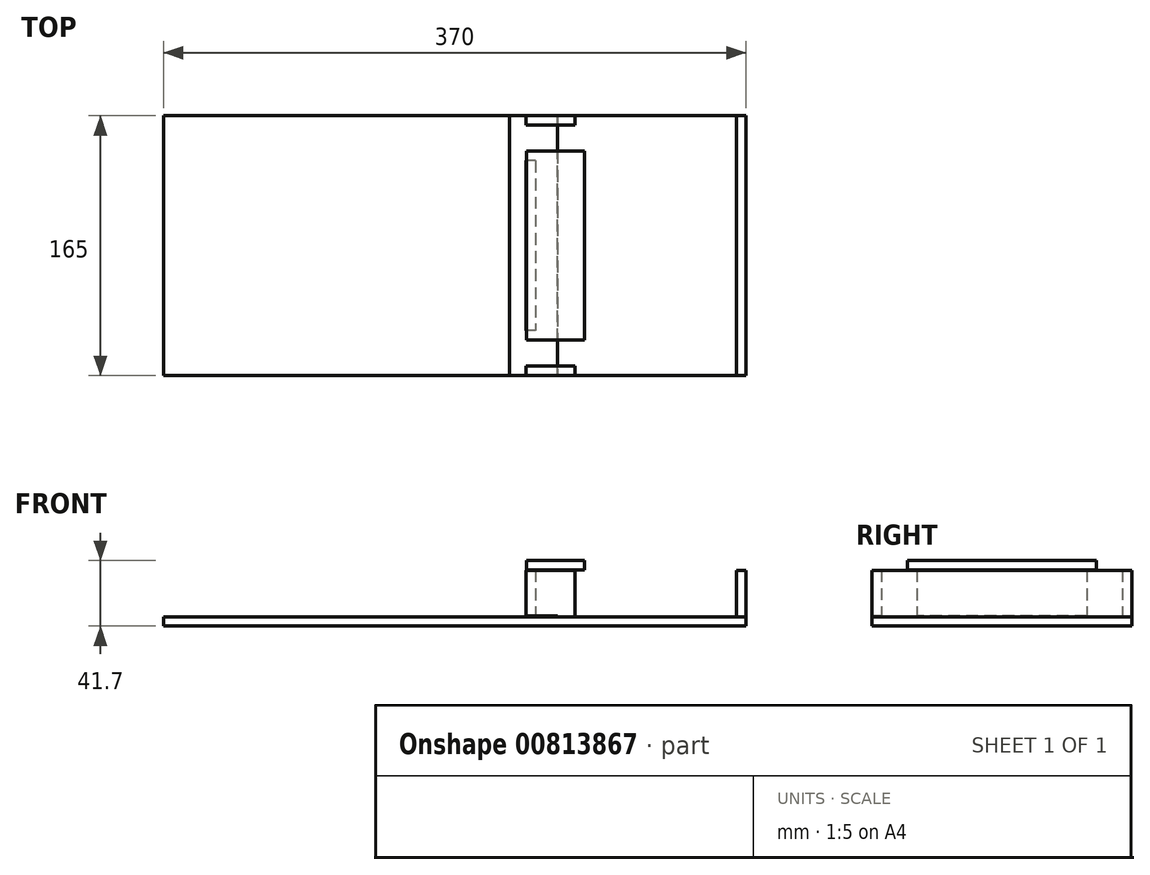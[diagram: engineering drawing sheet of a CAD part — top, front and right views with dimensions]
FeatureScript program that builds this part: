
annotation { "Feature Type Name" : "Feature", "Feature Type Description" : "" }
export const myFeature = defineFeature(function(context is Context, id is Id, definition is map)
    precondition{}
    {
        {
            var Q0;
            Q0=qCreatedBy(makeId("Top.planeOp"),FACE);
            var sketch = newSketch(context, id + "F0", { "sketchPlane" : qUnion([Q0])});
            skLineSegment(sketch, "E0.bottom", {"start": v(-185, 82.5) * mm, "end": v(185, 82.5) * mm});
            skLineSegment(sketch, "E0.top", {"start": v(-185, -82.5) * mm, "end": v(185, -82.5) * mm});
            skLineSegment(sketch, "E0.left", {"start": v(-185, 82.5) * mm, "end": v(-185, -82.5) * mm});
            skLineSegment(sketch, "E0.right", {"start": v(185, 82.5) * mm, "end": v(185, -82.5) * mm});
            skPoint(sketch, "E0.middle", {"position": v(0, 0) * mm});
            skSolve(sketch);
        }
        {
            var Q0;
            Q0 = qSketchRegion(id + "F0", true);
            extrude(context, id + "F1", {"entities" : qUnion([Q0]), "depth" : 6 * mm, "offsetDistance" : 25 * mm});
        }
        {
            var Q0;
            Q0=makeQuery(id+"F1.opExtrude","CAP_FACE",FACE,{"disambiguationData":[OSD([sQuery(id+"F0.wireOp",EDGE,"E0.bottom"),sQuery(id+"F0.wireOp",EDGE,"E0.top"),sQuery(id+"F0.wireOp",EDGE,"E0.left"),sQuery(id+"F0.wireOp",EDGE,"E0.right")])],"isStart":false});
            var sketch = newSketch(context, id + "F2", { "sketchPlane" : qUnion([Q0])});
            skLineSegment(sketch, "E1.bottom", {"start": v(185, 82.5) * mm, "end": v(179, 82.5) * mm});
            skLineSegment(sketch, "E1.top", {"start": v(185, -82.5) * mm, "end": v(179, -82.5) * mm});
            skLineSegment(sketch, "E1.left", {"start": v(185, 82.5) * mm, "end": v(185, -82.5) * mm});
            skLineSegment(sketch, "E1.right", {"start": v(179, 82.5) * mm, "end": v(179, -82.5) * mm});
            skSolve(sketch);
        }
        {
            var Q0;
            Q0 = qSketchRegion(id + "F2", true);
            extrude(context, id + "F3", {"entities" : qUnion([Q0]), "depth" : 29.5 * mm, "offsetDistance" : 25 * mm});
        }
        {
            var Q0;
            Q0=makeQuery(id+"F1.opExtrude","CAP_FACE",FACE,{"disambiguationData":[OSD([sQuery(id+"F0.wireOp",EDGE,"E0.bottom"),sQuery(id+"F0.wireOp",EDGE,"E0.top"),sQuery(id+"F0.wireOp",EDGE,"E0.left"),sQuery(id+"F0.wireOp",EDGE,"E0.right")])],"isStart":false});
            var sketch = newSketch(context, id + "F4", { "sketchPlane" : qUnion([Q0])});
            skLineSegment(sketch, "E2.bottom", {"start": v(76.46, -82.5) * mm, "end": v(45.46, -82.5) * mm});
            skLineSegment(sketch, "E2.top", {"start": v(76.46, -76.5) * mm, "end": v(45.46, -76.5) * mm});
            skLineSegment(sketch, "E2.left", {"start": v(76.46, -82.5) * mm, "end": v(76.46, -76.5) * mm});
            skLineSegment(sketch, "E2.right", {"start": v(45.46, -82.5) * mm, "end": v(45.46, -76.5) * mm});
            skLineSegment(sketch, "E3", {"start": v(-7.96, 0) * mm, "end": v(76.02, 0) * mm});
            skLineSegment(sketch, "E4.MirrorCS", {"start": v(76.46, 82.5) * mm, "end": v(45.46, 82.5) * mm});
            skLineSegment(sketch, "E5.MirrorCS", {"start": v(76.46, 76.5) * mm, "end": v(45.46, 76.5) * mm});
            skLineSegment(sketch, "E6.MirrorCS", {"start": v(45.46, 82.5) * mm, "end": v(45.46, 76.5) * mm});
            skLineSegment(sketch, "E7.MirrorCS", {"start": v(76.46, 82.5) * mm, "end": v(76.46, 76.5) * mm});
            skSolve(sketch);
        }
        {
            var Q0;
            Q0 = qSketchRegion(id + "F4", true);
            var Q1;
            Q1=makeQuery(id+"F3.opExtrude","CAP_FACE",FACE,{"disambiguationData":[OSD([sQuery(id+"F2.wireOp",EDGE,"E1.bottom"),sQuery(id+"F2.wireOp",EDGE,"E1.top"),sQuery(id+"F2.wireOp",EDGE,"E1.left"),sQuery(id+"F2.wireOp",EDGE,"E1.right")])],"isStart":false});
            extrude(context, id + "F5", {"entities" : qUnion([Q0]), "endBound" : BoundingType.UP_TO_SURFACE, "depth" : 27 * mm, "endBoundEntityFace" : qUnion([Q1]), "offsetDistance" : 25 * mm});
        }
        {
            var Q0;
            Q0=qCreatedBy(makeId("Front.planeOp"),FACE);
            var sketch = newSketch(context, id + "F6", { "sketchPlane" : qUnion([Q0])});
            skLineSegment(sketch, "E8.bottom", {"start": v(34.83, 5.98) * mm, "end": v(65.46, 5.98) * mm});
            skLineSegment(sketch, "E8.top", {"start": v(34.83, 6.48) * mm, "end": v(65.46, 6.48) * mm});
            skLineSegment(sketch, "E8.left", {"start": v(34.83, 5.98) * mm, "end": v(34.83, 6.48) * mm});
            skLineSegment(sketch, "E8.right", {"start": v(65.46, 5.98) * mm, "end": v(65.46, 6.48) * mm});
            skSolve(sketch);
        }
        {
            var Q0;
            Q0=makeQuery(id+"F6.imprint","IMPRINT",FACE,{"disambiguationData":[TD([[makeQuery(id+"F6.imprint","IMPRINT",EDGE,{"derivedFrom":sQuery(id+"F6.wireOp",EDGE,"E8.bottom")}),1.0]])]});
            extrude(context, id + "F7", {"entities" : qUnion([Q0]), "operationType" : NewBodyOperationType.REMOVE, "endBound" : BoundingType.SYMMETRIC, "oppositeDirection" : true, "depth" : 300 * mm, "offsetDistance" : 25 * mm});
        }
        {
            var Q0;
            Q0=qCreatedBy(makeId("Right.planeOp"),FACE);
            var Q1;
            Q1=makeQuery(id+"F5.opExtrude","CAP_VERTEX",VERTEX,{"disambiguationData":[OSD([sQuery(id+"F0.wireOp",EDGE,"E0.top"),sQuery(id+"F2.wireOp",EDGE,"E1.bottom"),sQuery(id+"F2.wireOp",EDGE,"E1.top"),sQuery(id+"F2.wireOp",EDGE,"E1.left"),sQuery(id+"F2.wireOp",EDGE,"E1.right"),sQuery(id+"F4.wireOp",EDGE,"E2.bottom"),sQuery(id+"F4.wireOp",EDGE,"E2.right")])],"isStart":false});
            cPlane(context, id + "F8", {"entities" : qUnion([Q0, Q1]), "cplaneType" : CPlaneType.PLANE_POINT, "offset" : 46 * mm, "width" : 150 * mm, "height" : 150 * mm});
        }
        {
            var Q0;
            Q0=qCreatedBy(id+"F8.planeOp",FACE);
            var sketch = newSketch(context, id + "F9", { "sketchPlane" : qUnion([Q0])});
            skLineSegment(sketch, "E9.bottom", {"start": v(54, 35.5) * mm, "end": v(-53.98, 35.5) * mm});
            skLineSegment(sketch, "E9.top", {"start": v(54, 6.48) * mm, "end": v(-53.98, 6.48) * mm});
            skLineSegment(sketch, "E9.left", {"start": v(54, 35.5) * mm, "end": v(54, 6.48) * mm});
            skLineSegment(sketch, "E9.right", {"start": v(-53.98, 35.5) * mm, "end": v(-53.98, 6.48) * mm});
            skSolve(sketch);
        }
        {
            var Q0;
            Q0 = qSketchRegion(id + "F9", true);
            extrude(context, id + "F10", {"entities" : qUnion([Q0]), "depth" : 6 * mm, "offsetDistance" : 25 * mm});
        }
        {
            var Q0;
            Q0=qCreatedBy(makeId("Top.planeOp"),FACE);
            cPlane(context, id + "F11", {"entities" : qUnion([Q0]), "cplaneType" : CPlaneType.OFFSET, "offset" : 35.7 * mm, "width" : 150 * mm, "height" : 150 * mm});
        }
        {
            var Q0;
            Q0=qCreatedBy(id+"F11.planeOp",FACE);
            var sketch = newSketch(context, id + "F12", { "sketchPlane" : qUnion([Q0])});
            skLineSegment(sketch, "E10.bottom", {"start": v(82.56, -60.05) * mm, "end": v(45.56, -60.05) * mm});
            skLineSegment(sketch, "E10.top", {"start": v(82.56, 60.16) * mm, "end": v(45.56, 60.16) * mm});
            skLineSegment(sketch, "E10.left", {"start": v(82.56, -60.05) * mm, "end": v(82.56, 60.16) * mm});
            skLineSegment(sketch, "E10.right", {"start": v(45.56, -60.05) * mm, "end": v(45.56, 60.16) * mm});
            skSolve(sketch);
        }
        {
            var Q0;
            Q0 = qSketchRegion(id + "F12", true);
            extrude(context, id + "F13", {"entities" : qUnion([Q0]), "depth" : 6 * mm, "offsetDistance" : 25 * mm});
        }
    });
